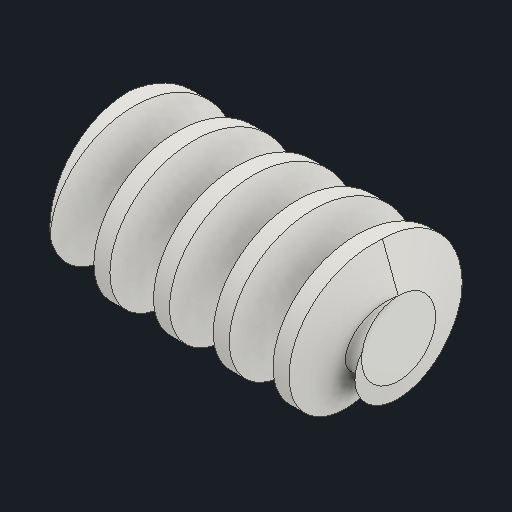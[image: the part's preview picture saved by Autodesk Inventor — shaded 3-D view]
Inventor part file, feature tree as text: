
AUTODESK INVENTOR PART (.ipt)
format: ipt  version: 2024 (Build 280153000, 153)  size: 273,408 bytes
history: native  units: mm (DEFAULTED — no unit token found)
features: other x5, chamfer x2, pattern_circular x2, extrude x1
ambient origin geometry x6: Origin, XZ Plane, X Axis, Y Axis, Z Axis, Center Point
bodies: Solid1 (feature_tree)
feature tree (10):
  extrude  "기본 본체"  Depth=40.0mm
  chamfer  "Chamfer1"  Distance=33.2mm
  chamfer  "Chamfer2"  Distance=60.0mm
  other  "톱니 스케치"
  pattern_circular  "톱니 패턴"  [2 undecoded]
  other  "왼쪽 톱니"
  pattern_circular  "왼쪽 톱니 패턴"  [2 undecoded]
  other  "기본 본체 스케치"
  other  "Srf1"
  other  "피치 지름"
note: 4 required parameter values undecoded (feature->parameter linkage not recoverable at this tier; creation-order binding heuristic only, values carry confidence <= 0.55)
